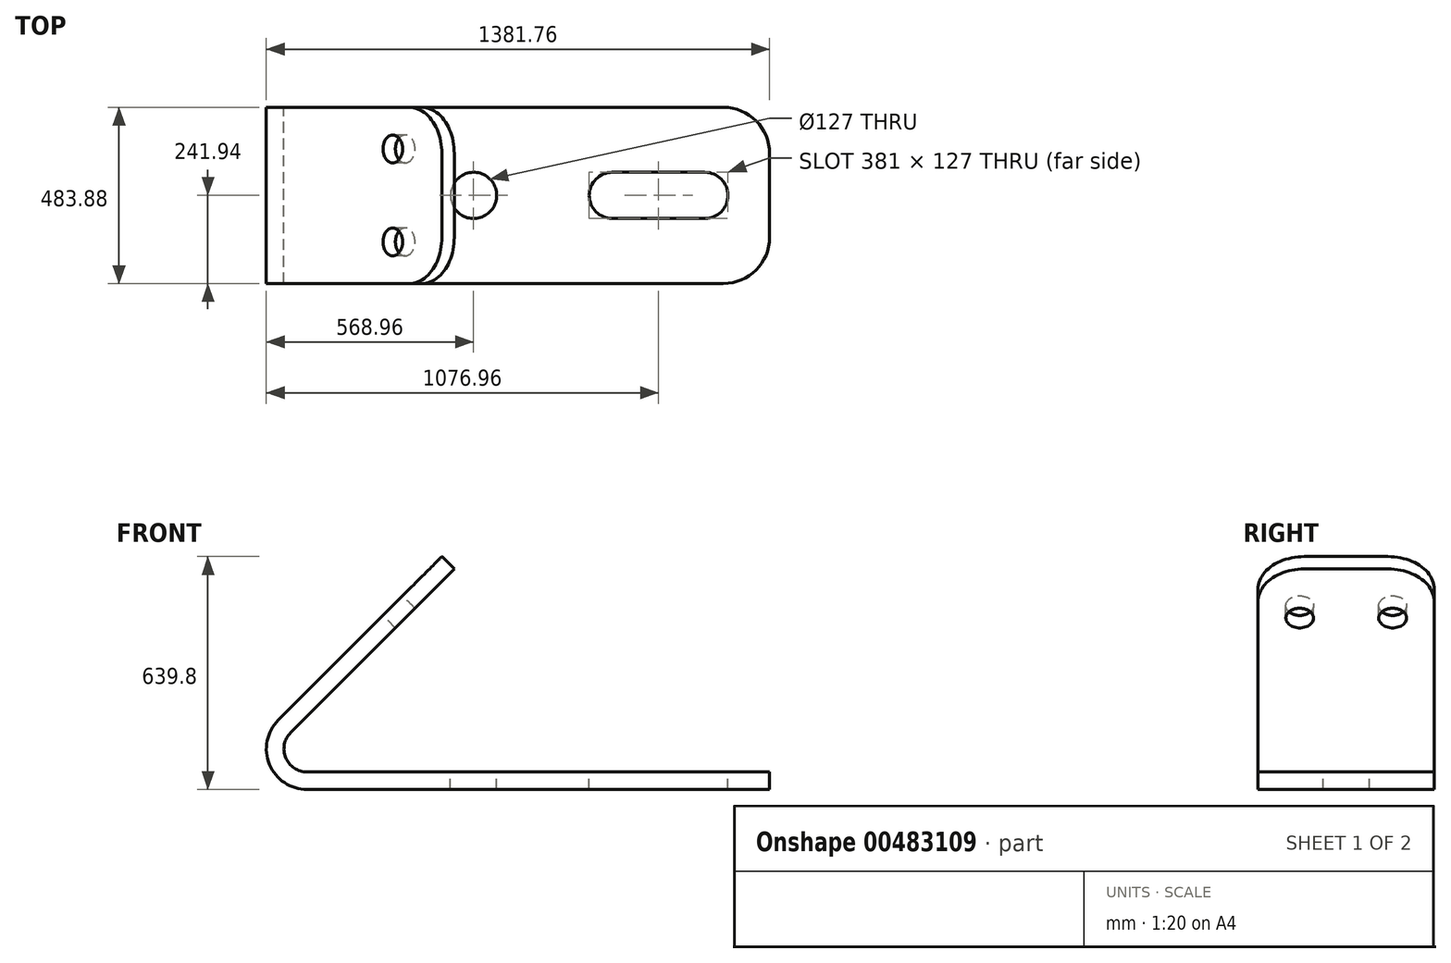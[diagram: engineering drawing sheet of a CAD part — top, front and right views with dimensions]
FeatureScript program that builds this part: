
annotation { "Feature Type Name" : "Feature", "Feature Type Description" : "" }
export const myFeature = defineFeature(function(context is Context, id is Id, definition is map)
    precondition{}
    {
        {
            var Q0;
            Q0=qCreatedBy(makeId("Front.planeOp"),FACE);
            var sketch = newSketch(context, id + "F0", { "sketchPlane" : qUnion([Q0])});
            skLineSegment(sketch, "E0", {"start": v(-635, 0) * mm, "end": v(635, 0) * mm});
            skLineSegment(sketch, "E1", {"start": v(-714.03, 190.79) * mm, "end": v(-265.01, 639.8) * mm});
            skArc(sketch, "E2.filletArc", {"start": v(-714.03, 190.79) * mm, "mid": v(-738.25, 69) * mm, "end": v(-635, 0) * mm});
            skLineSegment(sketch, "E3.0", {"start": v(-679.9, 156.66) * mm, "end": v(-230.89, 605.67) * mm});
            skArc(sketch, "E3.1", {"start": v(-679.9, 156.66) * mm, "mid": v(-693.67, 87.46) * mm, "end": v(-635, 48.26) * mm});
            skLineSegment(sketch, "E3.2", {"start": v(-635, 48.26) * mm, "end": v(635, 48.26) * mm});
            skLineSegment(sketch, "E4", {"start": v(635, 48.26) * mm, "end": v(635, 0) * mm});
            skLineSegment(sketch, "E5", {"start": v(-265.01, 639.8) * mm, "end": v(-230.89, 605.67) * mm});
            skSolve(sketch);
        }
        {
            var Q0;
            Q0 = qSketchRegion(id + "F0", true);
            extrude(context, id + "F1", {"entities" : qUnion([Q0]), "endBound" : BoundingType.SYMMETRIC, "depth" : 483.87 * mm});
        }
        {
            var Q0;
            Q0=makeQuery(id+"F1.opExtrude","SWEPT_FACE",FACE,{"disambiguationData":[OSD([sQuery(id+"F0.wireOp",EDGE,"E3.2")])]});
            var sketch = newSketch(context, id + "F2", { "sketchPlane" : qUnion([Q0])});
            skLineSegment(sketch, "E6", {"start": v(203.2, 0) * mm, "end": v(457.2, 0) * mm, "construction": true});
            skCircle(sketch, "E7", {"center": v(-177.8, 0) * mm, "radius": 63.5 * mm});
            skArc(sketch, "E8.0.startCap", {"start": v(203.2, -63.5) * mm, "mid": v(139.7, 0) * mm, "end": v(203.2, 63.5) * mm});
            skArc(sketch, "E8.0.endCap", {"start": v(457.2, 63.5) * mm, "mid": v(520.7, 0) * mm, "end": v(457.2, -63.5) * mm});
            skLineSegment(sketch, "E8.0.left", {"start": v(203.2, 63.5) * mm, "end": v(457.2, 63.5) * mm});
            skLineSegment(sketch, "E8.0.right", {"start": v(203.2, -63.5) * mm, "end": v(457.2, -63.5) * mm});
            skArc(sketch, "E9.filletArc", {"start": v(635, 114.94) * mm, "mid": v(597.8, 204.74) * mm, "end": v(508, 241.94) * mm});
            skLineSegment(sketch, "E10.0", {"start": v(508, 241.94) * mm, "end": v(635, 241.94) * mm});
            skLineSegment(sketch, "E11.0", {"start": v(635, 114.94) * mm, "end": v(635, 241.94) * mm});
            skArc(sketch, "E12.MirrorCS", {"start": v(635, -114.94) * mm, "mid": v(597.8, -204.74) * mm, "end": v(508, -241.94) * mm});
            skLineSegment(sketch, "E13.MirrorCS", {"start": v(635, -114.94) * mm, "end": v(635, -241.94) * mm});
            skLineSegment(sketch, "E14.MirrorCS", {"start": v(508, -241.94) * mm, "end": v(635, -241.94) * mm});
            skSolve(sketch);
        }
        {
            var Q0;
            Q0 = qSketchRegion(id + "F2", true);
            extrude(context, id + "F3", {"entities" : qUnion([Q0]), "operationType" : NewBodyOperationType.REMOVE, "endBound" : BoundingType.THROUGH_ALL, "oppositeDirection" : true, "depth" : 25.4 * mm});
        }
        {
            var Q0;
            Q0=makeQuery(id+"F1.opExtrude","SWEPT_FACE",FACE,{"disambiguationData":[OSD([sQuery(id+"F0.wireOp",EDGE,"E1")])]});
            var sketch = newSketch(context, id + "F4", { "sketchPlane" : qUnion([Q0])});
            skArc(sketch, "E15.filletArc", {"start": v(-114.94, 265.01) * mm, "mid": v(-204.74, 227.82) * mm, "end": v(-241.94, 138.01) * mm});
            skArc(sketch, "E16.filletArc", {"start": v(241.94, 138.01) * mm, "mid": v(204.74, 227.82) * mm, "end": v(114.94, 265.01) * mm});
            skLineSegment(sketch, "E17.1", {"start": v(-241.94, 138.01) * mm, "end": v(-241.94, 265.01) * mm});
            skLineSegment(sketch, "E17.2", {"start": v(241.94, 138.01) * mm, "end": v(241.94, 265.01) * mm});
            skLineSegment(sketch, "E18.trimOffspring", {"start": v(-114.94, 265.01) * mm, "end": v(-241.94, 265.01) * mm});
            skCircle(sketch, "E19", {"center": v(127.64, 74.51) * mm, "radius": 38.1 * mm});
            skLineSegment(sketch, "E20", {"start": v(0, 71.04) * mm, "end": v(0, -193.59) * mm, "construction": true});
            skCircle(sketch, "E21.MirrorC", {"center": v(-127.64, 74.51) * mm, "radius": 38.1 * mm});
            skSolve(sketch);
        }
        {
            var Q0;
            Q0 = qSketchRegion(id + "F4", true);
            var Q1;
            {var subQ0=sQuery(id+"F4.wireOp",EDGE,"E16.filletArc");Q1=makeQuery(id+"F4.imprint","IMPRINT",FACE,{"disambiguationData":[TD([[makeQuery(id+"F4.imprint","IMPRINT",EDGE,{"derivedFrom":subQ0}),-1.0]])]});}
            extrude(context, id + "F5", {"entities" : qUnion([Q0, Q1]), "operationType" : NewBodyOperationType.REMOVE, "endBound" : BoundingType.UP_TO_NEXT, "oppositeDirection" : true, "depth" : 25.4 * mm});
        }
    });
